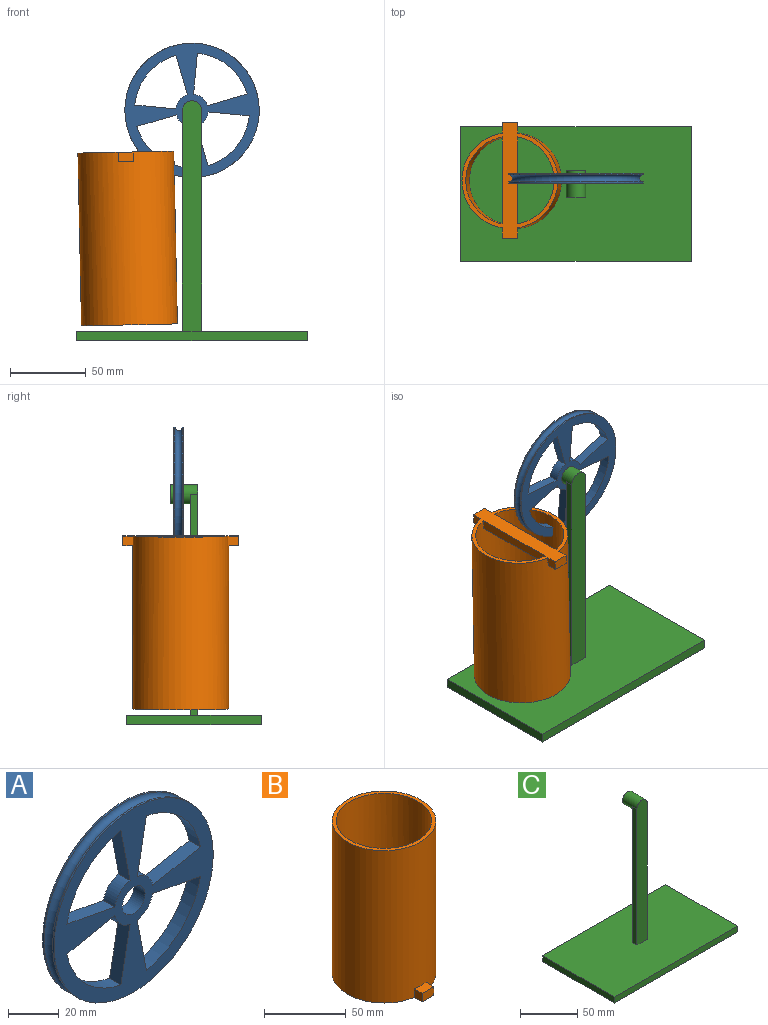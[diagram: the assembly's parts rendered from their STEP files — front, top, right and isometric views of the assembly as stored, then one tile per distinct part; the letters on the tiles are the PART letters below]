
ASSEMBLY  parts=3 mates=1
PART A: 22 faces, bbox 99.9x6.4x99.9 mm
  f0: cylinder r=44.45mm len=88.9mm, axis (0,1,0), area 221.7mm2, adj f19,f21
  f1: plane 26.76x6.35mm, normal (-0.19,0,0.98), area 173mm2, adj f2,f18,f19,f20
  f2: cylinder r=10.76mm len=8.55mm, axis (0,1,0), area 81.6mm2, adj f1,f3,f19,f20
  f3: plane 26.76x6.35mm, normal (0.98,0,-0.19), area 173mm2, adj f2,f18,f19,f20
  f4: plane 26.76x6.35mm, normal (-0.98,0,-0.19), area 173mm2, adj f5,f13,f19,f20
  f5: cylinder r=10.76mm len=8.55mm, axis (0,1,0), area 81.6mm2, adj f4,f6,f19,f20
  f6: plane 26.76x6.35mm, normal (0.19,0,0.98), area 173mm2, adj f5,f13,f19,f20
  f7: plane 26.76x6.35mm, normal (0.98,0,0.19), area 173mm2, adj f8,f14,f19,f20
  f8: cylinder r=10.76mm len=8.55mm, axis (0,1,0), area 81.6mm2, adj f7,f9,f19,f20
  f9: plane 26.76x6.35mm, normal (-0.19,0,-0.98), area 173mm2, adj f8,f14,f19,f20
  f10: cylinder r=38mm len=30.16mm, axis (0,1,0), area 286.5mm2, adj f11,f17,f19,f20
  f11: plane 26.73x6.35mm, normal (0.19,0,-0.98), area 173mm2, adj f10,f12,f19,f20
  f12: cylinder r=10.76mm len=8.54mm, axis (0,1,0), area 81.1mm2, adj f11,f17,f19,f20
  f13: cylinder r=38mm len=30.21mm, axis (0,1,0), area 288.1mm2, adj f4,f6,f19,f20
  f14: cylinder r=38mm len=30.21mm, axis (0,1,0), area 288.1mm2, adj f7,f9,f19,f20
  f15: cylinder r=44.45mm len=88.9mm, axis (0,1,0), area 221.7mm2, adj f20,f21
  f16: cylinder r=6.35mm len=12.7mm, axis (0,1,0), area 253.4mm2, adj f19,f20
  f17: plane 26.76x6.35mm, normal (-0.98,0,0.19), area 173mm2, adj f10,f12,f19,f20
  f18: cylinder r=38mm len=30.21mm, axis (0,1,0), area 288.1mm2, adj f1,f3,f19,f20
  f19: plane 88.9x88.9mm, normal (0,-1,0), area 2913.3mm2, adj f0,f1,f2,f3,f4,f5,f6,f7
  f20: plane 88.9x88.9mm, normal (0,1,0), area 2913.3mm2, adj f1,f2,f3,f4,f5,f6,f7,f8
  f21: torus R=44.44mm, axis (0,-1,0), area 2021.9mm2, adj f0,f15
PART B: 15 faces, bbox 63.5x76.4x114.3 mm
  f0: cylinder r=29.21mm len=114.3mm, axis (0,0,1), area 20848mm2, adj f2,f11,f12,f13,f14
  f1: cylinder r=31.75mm len=114.3mm, axis (0,0,1), area 22672.2mm2, adj f2,f3,f5,f6,f7,f8,f10,f14
  f2: plane 76.41x63.5mm, normal (0,0,-1), area 1210.9mm2, adj f0,f1,f3,f4,f5,f7,f8,f9
  f3: plane 6.86x6.35mm, normal (1,0,0), area 43.6mm2, adj f1,f2,f4,f6
  f4: plane 10.16x6.35mm, normal (0,-1,0), area 64.5mm2, adj f2,f3,f5,f6
  f5: plane 6.86x6.35mm, normal (-1,0,0), area 43.6mm2, adj f1,f2,f4,f6
  f6: plane 10.16x6.86mm, normal (0,0,1), area 66.9mm2, adj f1,f3,f4,f5
  f7: plane 6.86x6.35mm, normal (1,0,0), area 43.6mm2, adj f1,f2,f9,f10
  f8: plane 6.86x6.35mm, normal (-1,0,0), area 43.6mm2, adj f1,f2,f9,f10
  f9: plane 10.16x6.35mm, normal (0,1,0), area 64.5mm2, adj f2,f7,f8,f10
  f10: plane 10.16x6.86mm, normal (0,0,1), area 66.9mm2, adj f1,f7,f8,f9
  f11: plane 57.53x6.35mm, normal (1,0,0), area 365.3mm2, adj f0,f2,f13
  f12: plane 57.53x6.35mm, normal (-1,0,0), area 365.3mm2, adj f0,f2,f13
  f13: plane 58.42x10.16mm, normal (0,0,1), area 590.5mm2, adj f0,f11,f12
  f14: plane 63.5x63.5mm, normal (0,0,1), area 486.4mm2, adj f0,f1
PART C: 12 faces, bbox 152.4x88.9x158.8 mm
  f0: plane 146.05x12.7mm, normal (0,1,0), area 1791.5mm2, adj f1,f2,f4,f6
  f1: plane 146.05x5.08mm, normal (-1,0,0), area 741.9mm2, adj f0,f3,f4,f6
  f2: plane 146.05x5.08mm, normal (1,0,0), area 741.9mm2, adj f0,f3,f4,f6
  f3: plane 152.4x12.7mm, normal (0,-1,0), area 1918.2mm2, adj f1,f2,f4,f6
  f4: cylinder r=6.35mm len=17.78mm, axis (0,1,0), area 608mm2, adj f0,f1,f2,f3,f5
  f5: plane 12.7x12.7mm, normal (0,1,0), area 126.7mm2, adj f4
  f6: plane 152.4x88.9mm, normal (0,0,1), area 13483.8mm2, adj f0,f1,f2,f3,f7,f8,f9,f10
  f7: plane 152.4x6.35mm, normal (0,-1,0), area 967.7mm2, adj f6,f8,f10,f11
  f8: plane 88.9x6.35mm, normal (-1,0,0), area 564.5mm2, adj f6,f7,f9,f11
  f9: plane 152.4x6.35mm, normal (0,1,0), area 967.7mm2, adj f6,f8,f10,f11
  f10: plane 88.9x6.35mm, normal (1,0,0), area 564.5mm2, adj f6,f7,f9,f11
  f11: plane 152.4x88.9mm, normal (0,0,-1), area 13548.4mm2, adj f7,f8,f9,f10
PLACE A rot(axis=(0,1,0),174.6deg) t=(-75.38,-5.08,-4.51)mm
PLACE B rot(axis=(0,1,0),178.8deg) t=(-116.22,-44.61,-171.79)mm
PLACE C t=(-75.38,0,-4.51)mm
MATE revolute A.f16 <-> C.f4  axis (0,1,0) through (-75.38,-1.9,-4.51)mm
